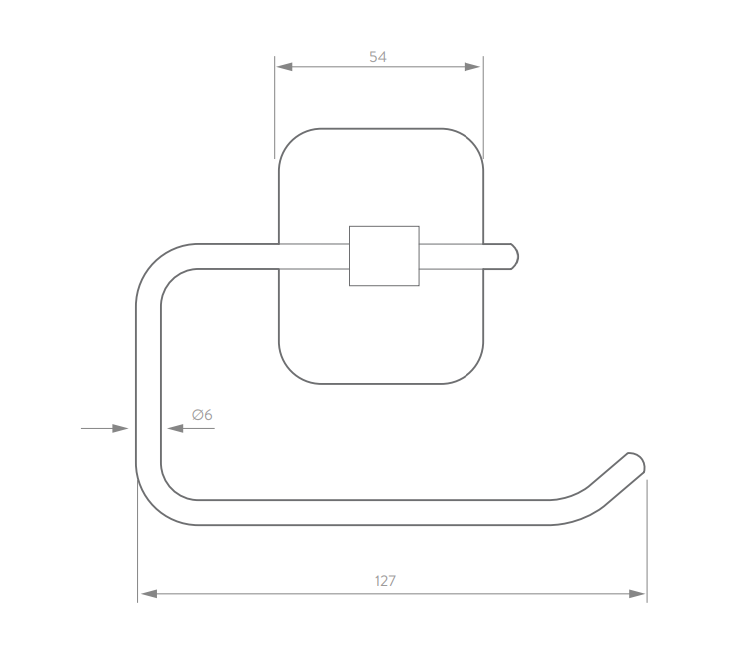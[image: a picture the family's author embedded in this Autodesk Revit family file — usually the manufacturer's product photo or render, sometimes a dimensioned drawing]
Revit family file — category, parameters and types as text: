
# Revit family: PM1055551_Portarrollo Palma
name_source: partatom
category: Plumbing Fixtures
units: mm (PartAtom-declared; Revit-internal decimal feet)

## family parameters
Always vertical = Yes
Cut with Voids When Loaded = No
Host = Wall
OmniClass Number = 23.19.31.17.11
OmniClass Title = Bathroom Units
Part Type = Normal
Room Calculation Point = No
Round Connector Dimension = Use Diameter
Shared = No

## types (1)
- Portarrollo Palma
    Alto = 104 mm
    Ancho = 127 mm
    Creado por = BIMBAU
    Default Elevation = 0 mm  [stored 0 ft]
    Description = Accesorios que reflejan las últimas tendencias de diseño convirtiéndose así en el mejor complemento para su baño. Contando con un sistema de instalación oculto en material metálico cromado que facilitan su limpieza y mantienen el diseño estilizado.
    Dimensiones generales del producto = 75 x 220 x 680 mm.
    Fecha de creación = 04/05/2021
    Garantía = 3 años - 3 años Cromado.
    Manufacturer = Corona.
    Material = Corona_Cromado
    Model = PM1055551_Portarrollo Palma.
    Peso Neto aprox = 1090 gr. (2.4030 lb).
    Profundidad = 32 mm  [stored 0.104987 ft]
    Recubrimientos = Resistente a la corrosión, pelado y decoloración por agua. Recubrimiento no tóxicos. Producto para uso doméstico.

note: [stored X ft] marks values corroborated as IEEE doubles in the binary element streams (Revit-internal decimal feet)

## geometry (parser evidence)
native form markers: Sweep x4
no freeform markers — native parametric forms only
